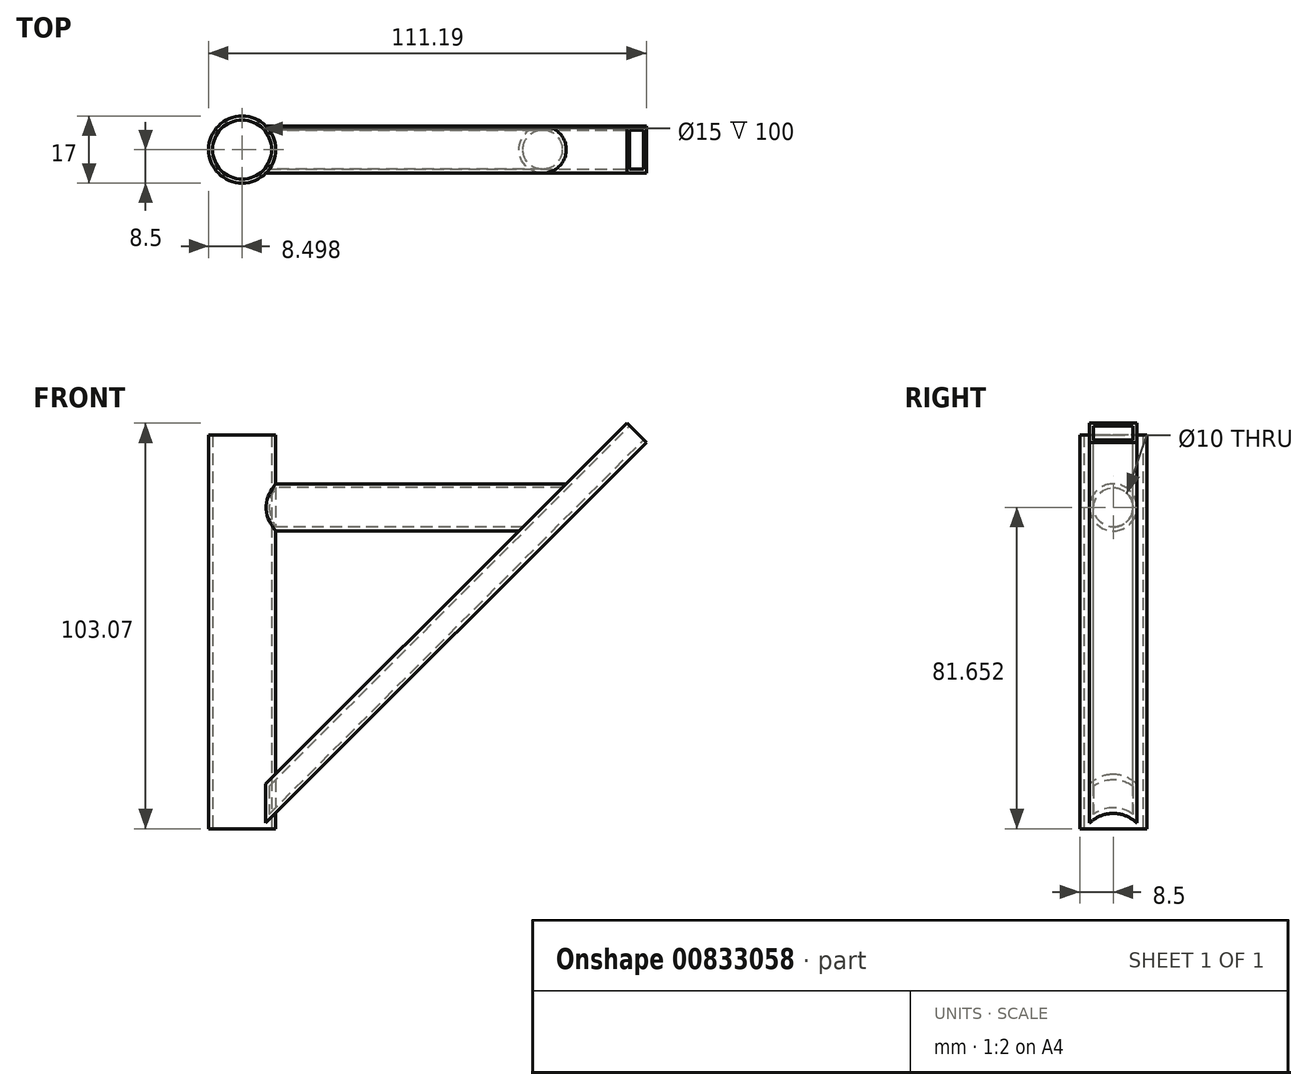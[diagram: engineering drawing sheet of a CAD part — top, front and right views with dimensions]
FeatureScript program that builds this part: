
annotation { "Feature Type Name" : "Feature", "Feature Type Description" : "" }
export const myFeature = defineFeature(function(context is Context, id is Id, definition is map)
    precondition{}
    {
        {
            var Q0;
            Q0=qCreatedBy(makeId("Top.planeOp"),FACE);
            var sketch = newSketch(context, id + "F0", { "sketchPlane" : qUnion([Q0])});
            skCircle(sketch, "E0", {"center": v(-24.03, 0) * mm, "radius": 7.5 * mm});
            skCircle(sketch, "E1.0", {"center": v(-24.03, 0) * mm, "radius": 8.5 * mm});
            skSolve(sketch);
        }
        {
            var Q0;
            Q0=makeQuery(id+"F0.imprint","IMPRINT",FACE,{"disambiguationData":[TD([[makeQuery(id+"F0.imprint","IMPRINT",EDGE,{"derivedFrom":sQuery(id+"F0.wireOp",EDGE,"E0")}),-1.0]])]});
            extrude(context, id + "F1", {"entities" : qUnion([Q0]), "depth" : 100 * mm, "offsetDistance" : 25 * mm});
        }
        {
            var Q0;
            Q0=qCreatedBy(makeId("Right.planeOp"),FACE);
            var sketch = newSketch(context, id + "F2", { "sketchPlane" : qUnion([Q0])});
            skCircle(sketch, "E2", {"center": v(0, 81.65) * mm, "radius": 5 * mm});
            skCircle(sketch, "E3.0", {"center": v(0, 81.65) * mm, "radius": 6 * mm});
            skSolve(sketch);
        }
        {
            var Q0;
            Q0 = qSketchRegion(id + "F2", true);
            extrude(context, id + "F3", {"entities" : qUnion([Q0]), "operationType" : NewBodyOperationType.ADD, "depth" : 25 * mm, "offsetDistance" : 25 * mm, "hasSecondDirection" : true, "secondDirectionBound" : SecondDirectionBoundingType.UP_TO_NEXT, "secondDirectionOppositeDirection" : true, "secondDirectionDepth" : 25 * mm});
        }
        {
            var Q0;
            Q0=qCreatedBy(makeId("Top.planeOp"),FACE);
            var sketch = newSketch(context, id + "F4", { "sketchPlane" : qUnion([Q0])});
            skLineSegment(sketch, "E4", {"start": v(0, 41.74) * mm, "end": v(0, -33.3) * mm});
            skSolve(sketch);
        }
        {
            var Q0;
            Q0=qCreatedBy(makeId("Top.planeOp"),FACE);
            var Q1;
            Q1=sQuery(id+"F4.wireOp",EDGE,"E4");
            cPlane(context, id + "F5", {"entities" : qUnion([Q0, Q1]), "cplaneType" : CPlaneType.LINE_ANGLE, "offset" : 25 * mm, "angle" : 315 * degree, "width" : 150 * mm, "height" : 150 * mm});
        }
        {
            var Q0;
            Q0=qCreatedBy(id+"F5.planeOp",FACE);
            var sketch = newSketch(context, id + "F6", { "sketchPlane" : qUnion([Q0])});
            skLineSegment(sketch, "E5.bottom", {"start": v(5, 19.76) * mm, "end": v(-5, 19.76) * mm});
            skLineSegment(sketch, "E5.top", {"start": v(5, 14.76) * mm, "end": v(-5, 14.76) * mm});
            skLineSegment(sketch, "E5.left", {"start": v(5, 19.76) * mm, "end": v(5, 14.76) * mm});
            skLineSegment(sketch, "E5.right", {"start": v(-5, 19.76) * mm, "end": v(-5, 14.76) * mm});
            skLineSegment(sketch, "E6.0", {"start": v(6, 13.76) * mm, "end": v(-6, 13.76) * mm});
            skLineSegment(sketch, "E6.1", {"start": v(6, 20.76) * mm, "end": v(6, 13.76) * mm});
            skLineSegment(sketch, "E6.2", {"start": v(6, 20.76) * mm, "end": v(-6, 20.76) * mm});
            skLineSegment(sketch, "E6.3", {"start": v(-6, 20.76) * mm, "end": v(-6, 13.76) * mm});
            skSolve(sketch);
        }
        {
            var Q0;
            Q0 = qSketchRegion(id + "F6", true);
            extrude(context, id + "F7", {"entities" : qUnion([Q0]), "operationType" : NewBodyOperationType.ADD, "endBound" : BoundingType.UP_TO_NEXT, "depth" : 25 * mm, "offsetDistance" : 25 * mm, "hasSecondDirection" : true, "secondDirectionOppositeDirection" : true, "secondDirectionDepth" : 125 * mm});
        }
        {
            var Q0;
            Q0=makeQuery(id+"F3.opExtrude","CAP_FACE",FACE,{"disambiguationData":[OSD([sQuery(id+"F2.wireOp",EDGE,"E2"),sQuery(id+"F2.wireOp",EDGE,"E3.0")])],"isStart":false});
            extrude(context, id + "F8", {"entities" : qUnion([Q0]), "operationType" : NewBodyOperationType.ADD, "endBound" : BoundingType.UP_TO_NEXT, "depth" : 25 * mm, "offsetDistance" : 25 * mm});
        }
    });
